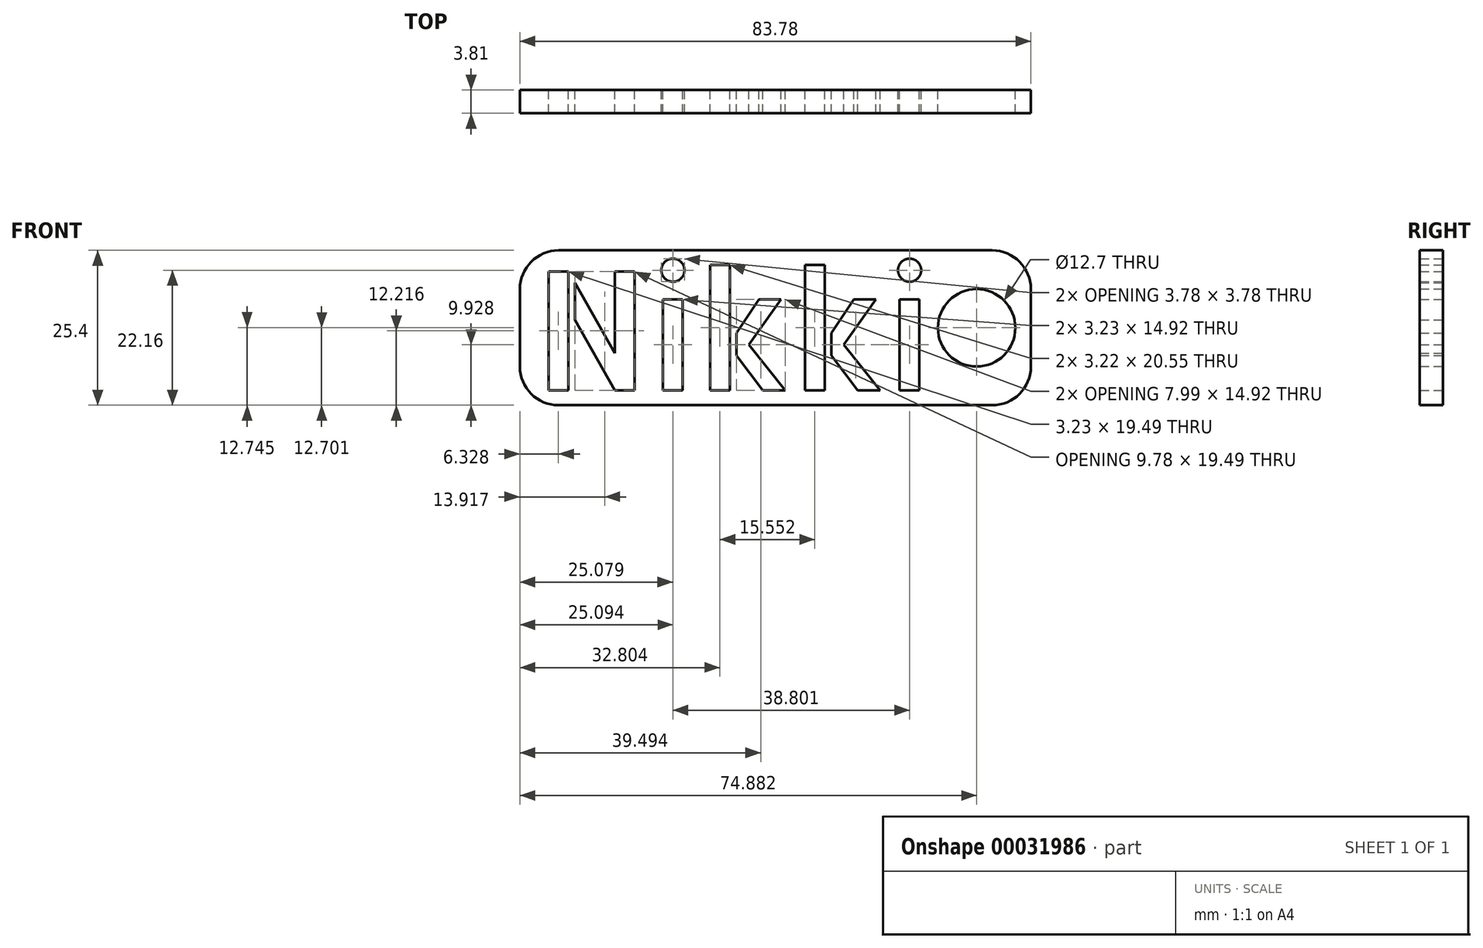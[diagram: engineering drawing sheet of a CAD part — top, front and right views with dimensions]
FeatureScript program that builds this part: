
annotation { "Feature Type Name" : "Feature", "Feature Type Description" : "" }
export const myFeature = defineFeature(function(context is Context, id is Id, definition is map)
    precondition{}
    {
        {
            var Q0;
            Q0=qCreatedBy(makeId("Front.planeOp"),FACE);
            var sketch = newSketch(context, id + "F0", { "sketchPlane" : qUnion([Q0])});
            skText(sketch, "E0", { "text": "Nikki", "fontName": "AllertaStencil-Regular.ttf"});
            skLineSegment(sketch, "E1", {"start": v(-41.35, 26.08) * mm, "end": v(-41.35, 13.38) * mm});
            skLineSegment(sketch, "E2", {"start": v(-35, 7.03) * mm, "end": v(36.08, 7.03) * mm});
            skLineSegment(sketch, "E3", {"start": v(42.43, 13.38) * mm, "end": v(42.43, 26.08) * mm});
            skLineSegment(sketch, "E4", {"start": v(-35, 32.43) * mm, "end": v(36.08, 32.43) * mm});
            skCircle(sketch, "E5", {"center": v(33.53, 19.73) * mm, "radius": 6.35 * mm});
            skPoint(sketch, "E5.centerSnap0", {"position": v(42.43, 19.73) * mm});
            skPoint(sketch, "E6.visualSharp", {"position": v(-41.35, 32.43) * mm});
            skArc(sketch, "E6.filletArc", {"start": v(-35, 32.43) * mm, "mid": v(-39.5, 30.57) * mm, "end": v(-41.35, 26.08) * mm});
            skPoint(sketch, "E7.visualSharp", {"position": v(42.43, 32.43) * mm});
            skArc(sketch, "E7.filletArc", {"start": v(42.43, 26.08) * mm, "mid": v(40.57, 30.57) * mm, "end": v(36.08, 32.43) * mm});
            skPoint(sketch, "E8.visualSharp", {"position": v(42.43, 7.03) * mm});
            skArc(sketch, "E8.filletArc", {"start": v(36.08, 7.03) * mm, "mid": v(40.57, 8.9) * mm, "end": v(42.43, 13.38) * mm});
            skPoint(sketch, "E9.visualSharp", {"position": v(-41.35, 7.03) * mm});
            skArc(sketch, "E9.filletArc", {"start": v(-41.35, 13.38) * mm, "mid": v(-39.5, 8.9) * mm, "end": v(-35, 7.03) * mm});
            const initialGuessF0  = {"E0": [-0.03907, 0.0095, 1, 0, 0.0195]};
            skSetInitialGuess(sketch, initialGuessF0);
            skSolve(sketch);
        }
        {
            var Q0;
            Q0=makeQuery(id+"F0.imprint","IMPRINT",FACE,{"disambiguationData":[TD([[makeQuery(id+"F0.imprint","IMPRINT",EDGE,{"derivedFrom":sQuery(id+"F0.wireOp",EDGE,"E0.sketch_text.stroke-0")}),1.0]])]});
            extrude(context, id + "F1", {"entities" : qUnion([Q0]), "depth" : 3.8 * mm});
        }
    });
